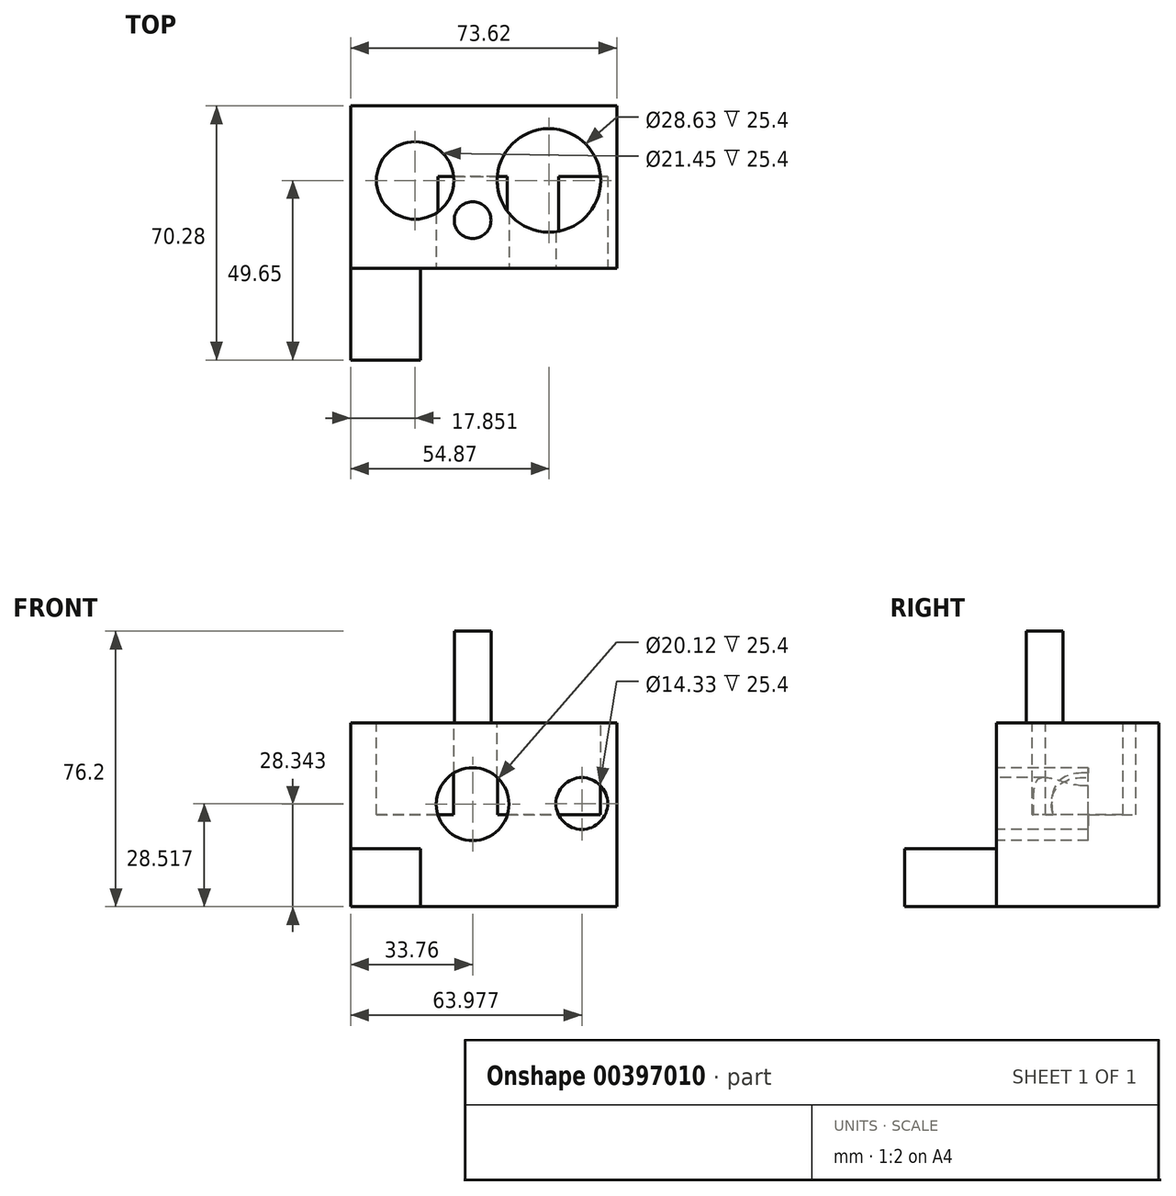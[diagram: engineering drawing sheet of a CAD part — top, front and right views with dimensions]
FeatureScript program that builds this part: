
annotation { "Feature Type Name" : "Feature", "Feature Type Description" : "" }
export const myFeature = defineFeature(function(context is Context, id is Id, definition is map)
    precondition{}
    {
        {
            var Q0;
            Q0=qCreatedBy(makeId("Top.planeOp"),FACE);
            var sketch = newSketch(context, id + "F0", { "sketchPlane" : qUnion([Q0])});
            skLineSegment(sketch, "E0.bottom", {"start": v(-33.76, 20.63) * mm, "end": v(39.86, 20.63) * mm});
            skLineSegment(sketch, "E0.top", {"start": v(-33.76, -24.25) * mm, "end": v(39.86, -24.25) * mm});
            skLineSegment(sketch, "E0.left", {"start": v(-33.76, 20.63) * mm, "end": v(-33.76, -24.25) * mm});
            skLineSegment(sketch, "E0.right", {"start": v(39.86, 20.63) * mm, "end": v(39.86, -24.25) * mm});
            skSolve(sketch);
        }
        {
            var Q0;
            Q0 = qSketchRegion(id + "F0", true);
            extrude(context, id + "F1", {"entities" : qUnion([Q0]), "depth" : 50.8 * mm});
        }
        {
            var Q0;
            Q0=makeQuery(id+"F1.opExtrude","CAP_FACE",FACE,{"disambiguationData":[OSD([sQuery(id+"F0.wireOp",EDGE,"E0.bottom"),sQuery(id+"F0.wireOp",EDGE,"E0.top"),sQuery(id+"F0.wireOp",EDGE,"E0.left"),sQuery(id+"F0.wireOp",EDGE,"E0.right")])],"isStart":false});
            var sketch = newSketch(context, id + "F2", { "sketchPlane" : qUnion([Q0])});
            skCircle(sketch, "E1", {"center": v(-15.9, 0) * mm, "radius": 10.72 * mm});
            skCircle(sketch, "E2", {"center": v(21.11, 0) * mm, "radius": 14.32 * mm});
            skSolve(sketch);
        }
        {
            var Q0;
            Q0 = qSketchRegion(id + "F2", true);
            extrude(context, id + "F3", {"entities" : qUnion([Q0]), "operationType" : NewBodyOperationType.REMOVE, "oppositeDirection" : true, "depth" : 25.4 * mm});
        }
        {
            var Q0;
            Q0=makeQuery(id+"F1.opExtrude","CAP_FACE",FACE,{"disambiguationData":[OSD([sQuery(id+"F0.wireOp",EDGE,"E0.bottom"),sQuery(id+"F0.wireOp",EDGE,"E0.top"),sQuery(id+"F0.wireOp",EDGE,"E0.left"),sQuery(id+"F0.wireOp",EDGE,"E0.right")])],"isStart":false});
            var sketch = newSketch(context, id + "F4", { "sketchPlane" : qUnion([Q0])});
            skCircle(sketch, "E3", {"center": v(0, -10.98) * mm, "radius": 5.08 * mm});
            skSolve(sketch);
        }
        {
            var Q0;
            Q0 = qSketchRegion(id + "F4", true);
            extrude(context, id + "F5", {"entities" : qUnion([Q0]), "operationType" : NewBodyOperationType.ADD, "depth" : 25.4 * mm});
        }
        {
            var Q0;
            Q0=makeQuery(id+"F1.opExtrude","SWEPT_FACE",FACE,{"disambiguationData":[OSD([sQuery(id+"F0.wireOp",EDGE,"E0.top")])]});
            var sketch = newSketch(context, id + "F6", { "sketchPlane" : qUnion([Q0])});
            skCircle(sketch, "E4", {"center": v(0, 28.34) * mm, "radius": 10.06 * mm});
            skSolve(sketch);
        }
        {
            var Q0;
            Q0 = qSketchRegion(id + "F6", true);
            extrude(context, id + "F7", {"entities" : qUnion([Q0]), "operationType" : NewBodyOperationType.REMOVE, "oppositeDirection" : true, "depth" : 25.4 * mm});
        }
        {
            var Q0;
            Q0=makeQuery(id+"F1.opExtrude","SWEPT_FACE",FACE,{"disambiguationData":[OSD([sQuery(id+"F0.wireOp",EDGE,"E0.top")])]});
            var sketch = newSketch(context, id + "F8", { "sketchPlane" : qUnion([Q0])});
            skCircle(sketch, "E5", {"center": v(30.22, 28.52) * mm, "radius": 7.16 * mm});
            skSolve(sketch);
        }
        {
            var Q0;
            Q0 = qSketchRegion(id + "F8", true);
            extrude(context, id + "F9", {"entities" : qUnion([Q0]), "operationType" : NewBodyOperationType.REMOVE, "oppositeDirection" : true, "depth" : 25.4 * mm});
        }
        {
            var Q0;
            Q0=makeQuery(id+"F1.opExtrude","SWEPT_FACE",FACE,{"disambiguationData":[OSD([sQuery(id+"F0.wireOp",EDGE,"E0.top")])]});
            var sketch = newSketch(context, id + "F10", { "sketchPlane" : qUnion([Q0])});
            skLineSegment(sketch, "E6.bottom", {"start": v(-33.76, 0) * mm, "end": v(-14.5, 0) * mm});
            skLineSegment(sketch, "E6.top", {"start": v(-33.76, 16.05) * mm, "end": v(-14.5, 16.05) * mm});
            skLineSegment(sketch, "E6.left", {"start": v(-33.76, 0) * mm, "end": v(-33.76, 16.05) * mm});
            skLineSegment(sketch, "E6.right", {"start": v(-14.5, 0) * mm, "end": v(-14.5, 16.05) * mm});
            skSolve(sketch);
        }
        {
            var Q0;
            Q0 = qSketchRegion(id + "F10", true);
            extrude(context, id + "F11", {"entities" : qUnion([Q0]), "operationType" : NewBodyOperationType.ADD, "depth" : 25.4 * mm});
        }
    });
